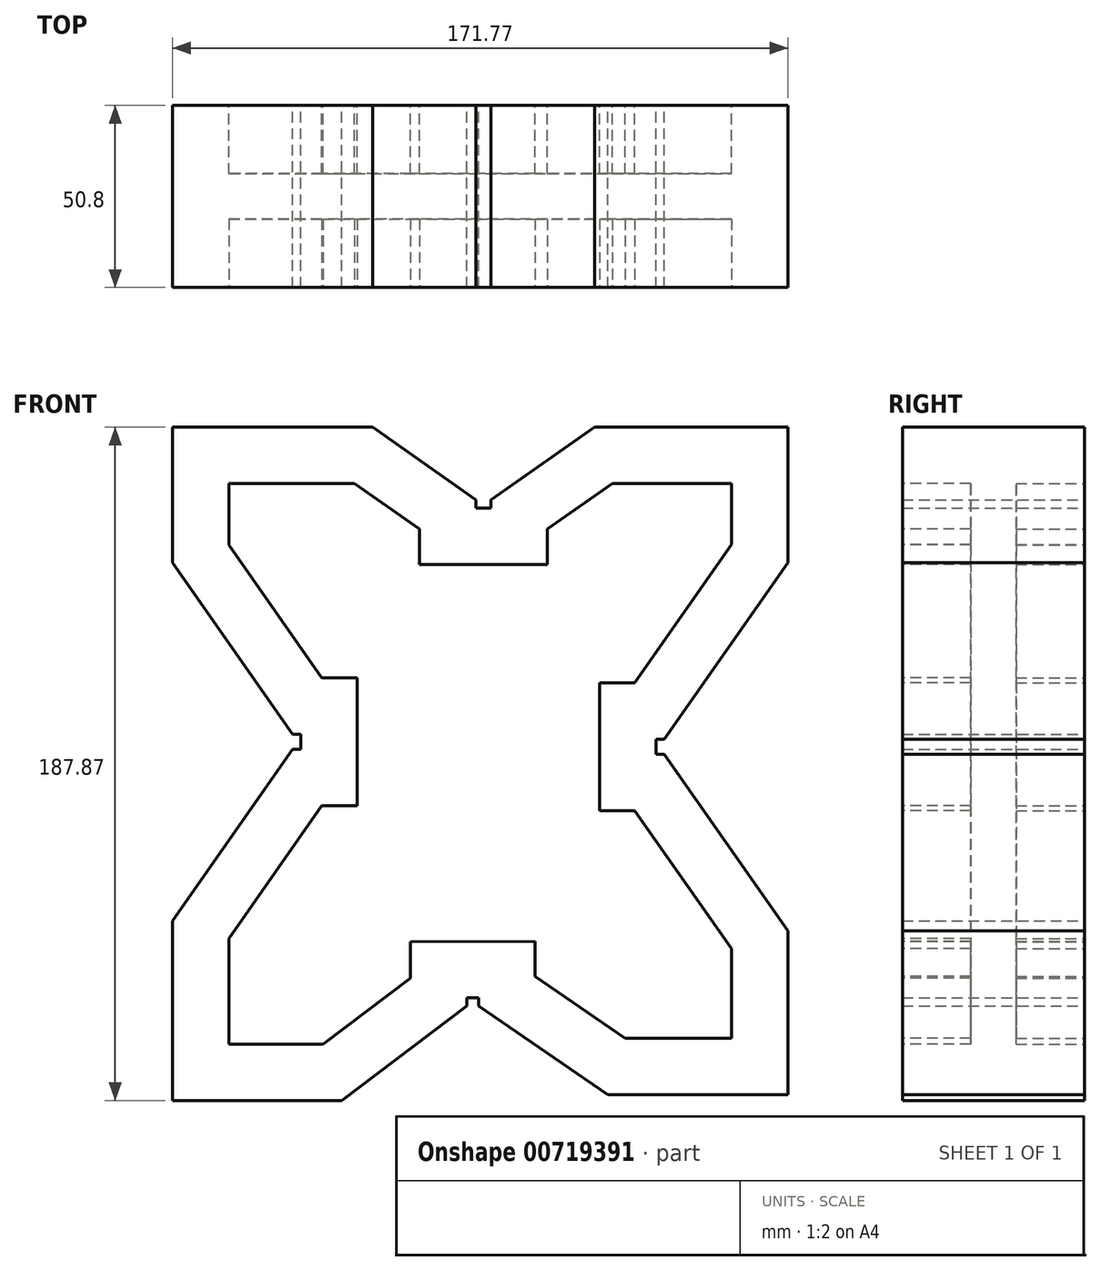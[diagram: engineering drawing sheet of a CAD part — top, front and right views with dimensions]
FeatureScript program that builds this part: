
annotation { "Feature Type Name" : "Feature", "Feature Type Description" : "" }
export const myFeature = defineFeature(function(context is Context, id is Id, definition is map)
    precondition{}
    {
        {
            var Q0;
            Q0=qCreatedBy(makeId("Front.planeOp"),FACE);
            var sketch = newSketch(context, id + "F0", { "sketchPlane" : qUnion([Q0])});
            skLineSegment(sketch, "E0", {"start": v(0, 2.31) * mm, "end": v(-28.9, 22.55) * mm});
            skLineSegment(sketch, "E1", {"start": v(-28.9, 22.55) * mm, "end": v(-84.7, 22.55) * mm});
            skLineSegment(sketch, "E2", {"start": v(-84.7, 22.55) * mm, "end": v(-84.7, -15.3) * mm});
            skLineSegment(sketch, "E3", {"start": v(33.12, 22.55) * mm, "end": v(4.22, 2.31) * mm});
            skLineSegment(sketch, "E4", {"start": v(4.22, 2.31) * mm, "end": v(4.22, 0) * mm});
            skLineSegment(sketch, "E5", {"start": v(33.12, 22.55) * mm, "end": v(87.07, 22.55) * mm});
            skLineSegment(sketch, "E6", {"start": v(87.07, 22.55) * mm, "end": v(87.07, -15.2) * mm});
            skLineSegment(sketch, "E7", {"start": v(0, 2.31) * mm, "end": v(0, 0) * mm});
            skLineSegment(sketch, "E8", {"start": v(87.07, -15.2) * mm, "end": v(52.55, -64.49) * mm});
            skLineSegment(sketch, "E9", {"start": v(52.55, -64.49) * mm, "end": v(50.24, -64.49) * mm});
            skLineSegment(sketch, "E10", {"start": v(50.24, -68.7) * mm, "end": v(52.55, -68.7) * mm});
            skLineSegment(sketch, "E11", {"start": v(52.55, -68.7) * mm, "end": v(87.07, -118) * mm});
            skLineSegment(sketch, "E12", {"start": v(87.07, -118) * mm, "end": v(87.07, -163.77) * mm});
            skLineSegment(sketch, "E13", {"start": v(87.07, -163.77) * mm, "end": v(36.75, -163.77) * mm});
            skLineSegment(sketch, "E14", {"start": v(-48.9, -67.35) * mm, "end": v(-51.21, -67.35) * mm});
            skLineSegment(sketch, "E15", {"start": v(-51.21, -67.35) * mm, "end": v(-84.7, -115.18) * mm});
            skLineSegment(sketch, "E16", {"start": v(-84.7, -115.18) * mm, "end": v(-84.7, -165.32) * mm});
            skLineSegment(sketch, "E17", {"start": v(-84.7, -165.32) * mm, "end": v(-37.43, -165.32) * mm});
            skLineSegment(sketch, "E18", {"start": v(-37.43, -165.32) * mm, "end": v(-2.5, -139) * mm});
            skLineSegment(sketch, "E19", {"start": v(-2.5, -139) * mm, "end": v(-2.5, -136.69) * mm});
            skLineSegment(sketch, "E20", {"start": v(-84.7, -15.3) * mm, "end": v(-51.21, -63.13) * mm});
            skLineSegment(sketch, "E21", {"start": v(-51.21, -63.13) * mm, "end": v(-48.9, -63.13) * mm});
            skLineSegment(sketch, "E22", {"start": v(36.75, -163.77) * mm, "end": v(0.7, -139) * mm});
            skLineSegment(sketch, "E23", {"start": v(0.7, -139) * mm, "end": v(0.7, -136.68) * mm});
            skLineSegment(sketch, "E24", {"start": v(0, 0) * mm, "end": v(4.22, 0) * mm});
            skLineSegment(sketch, "E25", {"start": v(-2.5, -136.69) * mm, "end": v(0.7, -136.68) * mm});
            skLineSegment(sketch, "E26", {"start": v(-48.9, -63.13) * mm, "end": v(-48.9, -67.35) * mm});
            skLineSegment(sketch, "E27", {"start": v(50.24, -64.49) * mm, "end": v(50.24, -68.7) * mm});
            skSolve(sketch);
        }
        {
            var Q0;
            Q0=makeQuery(id+"F0.imprint","IMPRINT",FACE,{"disambiguationData":[TD([[makeQuery(id+"F0.imprint","IMPRINT",EDGE,{"derivedFrom":sQuery(id+"F0.wireOp",EDGE,"E0")}),1.0]])]});
            extrude(context, id + "F1", {"entities" : qUnion([Q0]), "endBound" : BoundingType.SYMMETRIC, "depth" : 50.8 * mm, "offsetDistance" : 25.4 * mm});
        }
        {
            var Q0;
            Q0=makeQuery(id+"F1.opExtrude","CAP_FACE",FACE,{"disambiguationData":[OSD([sQuery(id+"F0.wireOp",EDGE,"E0"),sQuery(id+"F0.wireOp",EDGE,"E1"),sQuery(id+"F0.wireOp",EDGE,"E2"),sQuery(id+"F0.wireOp",EDGE,"E3"),sQuery(id+"F0.wireOp",EDGE,"E4"),sQuery(id+"F0.wireOp",EDGE,"E5"),sQuery(id+"F0.wireOp",EDGE,"E6"),sQuery(id+"F0.wireOp",EDGE,"E7"),sQuery(id+"F0.wireOp",EDGE,"E8"),sQuery(id+"F0.wireOp",EDGE,"E9"),sQuery(id+"F0.wireOp",EDGE,"E10"),sQuery(id+"F0.wireOp",EDGE,"E11"),sQuery(id+"F0.wireOp",EDGE,"E12"),sQuery(id+"F0.wireOp",EDGE,"E13"),sQuery(id+"F0.wireOp",EDGE,"E14"),sQuery(id+"F0.wireOp",EDGE,"E15"),sQuery(id+"F0.wireOp",EDGE,"E16"),sQuery(id+"F0.wireOp",EDGE,"E17"),sQuery(id+"F0.wireOp",EDGE,"E18"),sQuery(id+"F0.wireOp",EDGE,"E19"),sQuery(id+"F0.wireOp",EDGE,"E20"),sQuery(id+"F0.wireOp",EDGE,"E21"),sQuery(id+"F0.wireOp",EDGE,"E22"),sQuery(id+"F0.wireOp",EDGE,"E23"),sQuery(id+"F0.wireOp",EDGE,"E24"),sQuery(id+"F0.wireOp",EDGE,"E25"),sQuery(id+"F0.wireOp",EDGE,"E26"),sQuery(id+"F0.wireOp",EDGE,"E27")])],"isStart":false});
            var sketch = newSketch(context, id + "F2", { "sketchPlane" : qUnion([Q0])});
            skLineSegment(sketch, "E28.0", {"start": v(33.12, 22.55) * mm, "end": v(4.22, 2.31) * mm});
            skLineSegment(sketch, "E29.0", {"start": v(33.12, 22.55) * mm, "end": v(87.07, 22.55) * mm});
            skLineSegment(sketch, "E30.0", {"start": v(87.07, 22.55) * mm, "end": v(87.07, -15.2) * mm});
            skLineSegment(sketch, "E31.0", {"start": v(87.07, -15.2) * mm, "end": v(52.55, -64.49) * mm});
            skLineSegment(sketch, "E32.0.0", {"start": v(0.7, -139) * mm, "end": v(36.75, -163.77) * mm});
            skLineSegment(sketch, "E32.0.1", {"start": v(36.75, -163.77) * mm, "end": v(87.07, -163.77) * mm});
            skLineSegment(sketch, "E32.0.2", {"start": v(87.07, -163.77) * mm, "end": v(87.07, -118) * mm});
            skLineSegment(sketch, "E32.0.3", {"start": v(87.07, -118) * mm, "end": v(52.55, -68.7) * mm});
            skLineSegment(sketch, "E32.0.4", {"start": v(52.55, -68.7) * mm, "end": v(50.24, -68.7) * mm});
            skLineSegment(sketch, "E32.0.5", {"start": v(50.24, -68.7) * mm, "end": v(50.24, -64.49) * mm});
            skLineSegment(sketch, "E32.0.6", {"start": v(50.24, -64.49) * mm, "end": v(52.55, -64.49) * mm});
            skLineSegment(sketch, "E32.0.7", {"start": v(52.55, -64.49) * mm, "end": v(87.07, -15.2) * mm});
            skLineSegment(sketch, "E32.0.8", {"start": v(87.07, -15.2) * mm, "end": v(87.07, 22.55) * mm});
            skLineSegment(sketch, "E32.0.9", {"start": v(87.07, 22.55) * mm, "end": v(33.12, 22.55) * mm});
            skLineSegment(sketch, "E32.0.11", {"start": v(4.22, 2.31) * mm, "end": v(4.22, 0) * mm});
            skLineSegment(sketch, "E32.0.12", {"start": v(4.22, 0) * mm, "end": v(0, 0) * mm});
            skLineSegment(sketch, "E32.0.13", {"start": v(0, 0) * mm, "end": v(0, 2.31) * mm});
            skLineSegment(sketch, "E32.0.14", {"start": v(0, 2.31) * mm, "end": v(-28.9, 22.55) * mm});
            skLineSegment(sketch, "E32.0.15", {"start": v(-28.9, 22.55) * mm, "end": v(-84.7, 22.55) * mm});
            skLineSegment(sketch, "E32.0.16", {"start": v(-84.7, 22.55) * mm, "end": v(-84.7, -15.3) * mm});
            skLineSegment(sketch, "E32.0.17", {"start": v(-84.7, -15.3) * mm, "end": v(-51.21, -63.13) * mm});
            skLineSegment(sketch, "E32.0.18", {"start": v(-51.21, -63.13) * mm, "end": v(-48.9, -63.13) * mm});
            skLineSegment(sketch, "E32.0.19", {"start": v(-48.9, -63.13) * mm, "end": v(-48.9, -67.35) * mm});
            skLineSegment(sketch, "E32.0.20", {"start": v(-48.9, -67.35) * mm, "end": v(-51.21, -67.35) * mm});
            skLineSegment(sketch, "E32.0.21", {"start": v(-51.21, -67.35) * mm, "end": v(-84.7, -115.18) * mm});
            skLineSegment(sketch, "E32.0.22", {"start": v(-84.7, -115.18) * mm, "end": v(-84.7, -165.32) * mm});
            skLineSegment(sketch, "E32.0.23", {"start": v(-84.7, -165.32) * mm, "end": v(-37.43, -165.32) * mm});
            skLineSegment(sketch, "E32.0.24", {"start": v(-37.43, -165.32) * mm, "end": v(-2.5, -139) * mm});
            skLineSegment(sketch, "E32.0.25", {"start": v(-2.5, -139) * mm, "end": v(-2.5, -136.69) * mm});
            skLineSegment(sketch, "E32.0.26", {"start": v(-2.5, -136.69) * mm, "end": v(0.7, -136.68) * mm});
            skLineSegment(sketch, "E32.0.27", {"start": v(0.7, -136.68) * mm, "end": v(0.7, -139) * mm});
            skLineSegment(sketch, "E33.0", {"start": v(16.45, -120.89) * mm, "end": v(16.45, -130.7) * mm});
            skLineSegment(sketch, "E33.1", {"start": v(-18.25, -120.98) * mm, "end": v(16.45, -120.89) * mm});
            skLineSegment(sketch, "E33.2", {"start": v(-18.25, -131.15) * mm, "end": v(-18.25, -120.98) * mm});
            skLineSegment(sketch, "E33.3", {"start": v(-42.7, -149.57) * mm, "end": v(-18.25, -131.15) * mm});
            skLineSegment(sketch, "E33.4", {"start": v(-68.96, -149.57) * mm, "end": v(-42.7, -149.57) * mm});
            skLineSegment(sketch, "E33.5", {"start": v(38.08, 6.8) * mm, "end": v(19.96, -5.89) * mm});
            skLineSegment(sketch, "E33.6", {"start": v(71.32, 6.8) * mm, "end": v(38.08, 6.8) * mm});
            skLineSegment(sketch, "E33.7", {"start": v(71.32, -10.23) * mm, "end": v(71.32, 6.8) * mm});
            skLineSegment(sketch, "E33.8", {"start": v(44.35, -48.74) * mm, "end": v(71.32, -10.23) * mm});
            skLineSegment(sketch, "E33.9", {"start": v(34.5, -48.74) * mm, "end": v(44.35, -48.74) * mm});
            skLineSegment(sketch, "E33.10", {"start": v(34.5, -84.45) * mm, "end": v(34.5, -48.74) * mm});
            skLineSegment(sketch, "E33.11", {"start": v(41.64, -148.02) * mm, "end": v(71.32, -148.02) * mm});
            skLineSegment(sketch, "E33.12", {"start": v(71.32, -148.02) * mm, "end": v(71.32, -122.96) * mm});
            skLineSegment(sketch, "E33.13", {"start": v(71.32, -122.96) * mm, "end": v(44.35, -84.45) * mm});
            skLineSegment(sketch, "E33.14", {"start": v(44.35, -84.45) * mm, "end": v(34.5, -84.45) * mm});
            skLineSegment(sketch, "E33.15", {"start": v(19.96, -5.89) * mm, "end": v(19.96, -15.75) * mm});
            skLineSegment(sketch, "E33.16", {"start": v(19.96, -15.75) * mm, "end": v(-15.75, -15.75) * mm});
            skLineSegment(sketch, "E33.17", {"start": v(-15.75, -15.75) * mm, "end": v(-15.75, -5.89) * mm});
            skLineSegment(sketch, "E33.18", {"start": v(-15.75, -5.89) * mm, "end": v(-33.87, 6.8) * mm});
            skLineSegment(sketch, "E33.19", {"start": v(-33.87, 6.8) * mm, "end": v(-68.96, 6.8) * mm});
            skLineSegment(sketch, "E33.20", {"start": v(16.45, -130.7) * mm, "end": v(41.64, -148.02) * mm});
            skLineSegment(sketch, "E33.21", {"start": v(-68.96, 6.8) * mm, "end": v(-68.96, -10.33) * mm});
            skLineSegment(sketch, "E33.22", {"start": v(-68.96, -10.33) * mm, "end": v(-43.01, -47.38) * mm});
            skLineSegment(sketch, "E33.23", {"start": v(-43.01, -47.38) * mm, "end": v(-33.15, -47.38) * mm});
            skLineSegment(sketch, "E33.24", {"start": v(-33.15, -47.38) * mm, "end": v(-33.15, -83.1) * mm});
            skLineSegment(sketch, "E33.25", {"start": v(-33.15, -83.1) * mm, "end": v(-43.01, -83.1) * mm});
            skLineSegment(sketch, "E33.26", {"start": v(-43.01, -83.1) * mm, "end": v(-68.96, -120.15) * mm});
            skLineSegment(sketch, "E33.27", {"start": v(-68.96, -120.15) * mm, "end": v(-68.96, -149.57) * mm});
            skSolve(sketch);
        }
        {
            var Q0;
            Q0=makeQuery(id+"F2.imprint","IMPRINT",FACE,{"disambiguationData":[TD([[makeQuery(id+"F2.imprint","IMPRINT",EDGE,{"derivedFrom":sQuery(id+"F2.wireOp",EDGE,"E33.0")}),1.0]])]});
            extrude(context, id + "F3", {"entities" : qUnion([Q0]), "operationType" : NewBodyOperationType.REMOVE, "oppositeDirection" : true, "depth" : 19.05 * mm, "offsetDistance" : 25.4 * mm});
        }
        {
            var Q0;
            Q0=makeQuery(id+"F1.opExtrude","CAP_FACE",FACE,{"disambiguationData":[OSD([sQuery(id+"F0.wireOp",EDGE,"E0"),sQuery(id+"F0.wireOp",EDGE,"E1"),sQuery(id+"F0.wireOp",EDGE,"E2"),sQuery(id+"F0.wireOp",EDGE,"E3"),sQuery(id+"F0.wireOp",EDGE,"E4"),sQuery(id+"F0.wireOp",EDGE,"E5"),sQuery(id+"F0.wireOp",EDGE,"E6"),sQuery(id+"F0.wireOp",EDGE,"E7"),sQuery(id+"F0.wireOp",EDGE,"E8"),sQuery(id+"F0.wireOp",EDGE,"E9"),sQuery(id+"F0.wireOp",EDGE,"E10"),sQuery(id+"F0.wireOp",EDGE,"E11"),sQuery(id+"F0.wireOp",EDGE,"E12"),sQuery(id+"F0.wireOp",EDGE,"E13"),sQuery(id+"F0.wireOp",EDGE,"E14"),sQuery(id+"F0.wireOp",EDGE,"E15"),sQuery(id+"F0.wireOp",EDGE,"E16"),sQuery(id+"F0.wireOp",EDGE,"E17"),sQuery(id+"F0.wireOp",EDGE,"E18"),sQuery(id+"F0.wireOp",EDGE,"E19"),sQuery(id+"F0.wireOp",EDGE,"E20"),sQuery(id+"F0.wireOp",EDGE,"E21"),sQuery(id+"F0.wireOp",EDGE,"E22"),sQuery(id+"F0.wireOp",EDGE,"E23"),sQuery(id+"F0.wireOp",EDGE,"E24"),sQuery(id+"F0.wireOp",EDGE,"E25"),sQuery(id+"F0.wireOp",EDGE,"E26"),sQuery(id+"F0.wireOp",EDGE,"E27")])],"isStart":true});
            var sketch = newSketch(context, id + "F4", { "sketchPlane" : qUnion([Q0])});
            skLineSegment(sketch, "E34.0.0", {"start": v(-36.75, -163.77) * mm, "end": v(-0.7, -139) * mm});
            skLineSegment(sketch, "E34.0.1", {"start": v(-0.7, -139) * mm, "end": v(-0.7, -136.68) * mm});
            skLineSegment(sketch, "E34.0.2", {"start": v(-0.7, -136.68) * mm, "end": v(2.5, -136.69) * mm});
            skLineSegment(sketch, "E34.0.3", {"start": v(2.5, -136.69) * mm, "end": v(2.5, -139) * mm});
            skLineSegment(sketch, "E34.0.4", {"start": v(2.5, -139) * mm, "end": v(37.43, -165.32) * mm});
            skLineSegment(sketch, "E34.0.5", {"start": v(37.43, -165.32) * mm, "end": v(84.7, -165.32) * mm});
            skLineSegment(sketch, "E34.0.6", {"start": v(84.7, -165.32) * mm, "end": v(84.7, -115.18) * mm});
            skLineSegment(sketch, "E34.0.7", {"start": v(84.7, -115.18) * mm, "end": v(51.21, -67.35) * mm});
            skLineSegment(sketch, "E34.0.8", {"start": v(51.21, -67.35) * mm, "end": v(48.9, -67.35) * mm});
            skLineSegment(sketch, "E34.0.9", {"start": v(48.9, -67.35) * mm, "end": v(48.9, -63.13) * mm});
            skLineSegment(sketch, "E34.0.10", {"start": v(48.9, -63.13) * mm, "end": v(51.21, -63.13) * mm});
            skLineSegment(sketch, "E34.0.11", {"start": v(51.21, -63.13) * mm, "end": v(84.7, -15.3) * mm});
            skLineSegment(sketch, "E34.0.12", {"start": v(84.7, -15.3) * mm, "end": v(84.7, 22.55) * mm});
            skLineSegment(sketch, "E34.0.13", {"start": v(84.7, 22.55) * mm, "end": v(28.9, 22.55) * mm});
            skLineSegment(sketch, "E34.0.14", {"start": v(28.9, 22.55) * mm, "end": v(0, 2.31) * mm});
            skLineSegment(sketch, "E34.0.15", {"start": v(0, 2.31) * mm, "end": v(0, 0) * mm});
            skLineSegment(sketch, "E34.0.16", {"start": v(0, 0) * mm, "end": v(-4.22, 0) * mm});
            skLineSegment(sketch, "E34.0.17", {"start": v(-4.22, 0) * mm, "end": v(-4.22, 2.31) * mm});
            skLineSegment(sketch, "E34.0.18", {"start": v(-4.22, 2.31) * mm, "end": v(-33.12, 22.55) * mm});
            skLineSegment(sketch, "E34.0.19", {"start": v(-33.12, 22.55) * mm, "end": v(-87.07, 22.55) * mm});
            skLineSegment(sketch, "E34.0.20", {"start": v(-87.07, 22.55) * mm, "end": v(-87.07, -15.2) * mm});
            skLineSegment(sketch, "E34.0.21", {"start": v(-87.07, -15.2) * mm, "end": v(-52.55, -64.49) * mm});
            skLineSegment(sketch, "E34.0.22", {"start": v(-52.55, -64.49) * mm, "end": v(-50.24, -64.49) * mm});
            skLineSegment(sketch, "E34.0.23", {"start": v(-50.24, -64.49) * mm, "end": v(-50.24, -68.7) * mm});
            skLineSegment(sketch, "E34.0.24", {"start": v(-50.24, -68.7) * mm, "end": v(-52.55, -68.7) * mm});
            skLineSegment(sketch, "E34.0.25", {"start": v(-52.55, -68.7) * mm, "end": v(-87.07, -118) * mm});
            skLineSegment(sketch, "E34.0.26", {"start": v(-87.07, -118) * mm, "end": v(-87.07, -163.77) * mm});
            skLineSegment(sketch, "E34.0.27", {"start": v(-87.07, -163.77) * mm, "end": v(-36.75, -163.77) * mm});
            skLineSegment(sketch, "E35.0", {"start": v(-71.32, -148.02) * mm, "end": v(-41.64, -148.02) * mm});
            skLineSegment(sketch, "E35.1", {"start": v(-71.32, -122.96) * mm, "end": v(-71.32, -148.02) * mm});
            skLineSegment(sketch, "E35.2", {"start": v(-44.35, -84.45) * mm, "end": v(-71.32, -122.96) * mm});
            skLineSegment(sketch, "E35.3", {"start": v(-34.5, -84.45) * mm, "end": v(-44.35, -84.45) * mm});
            skLineSegment(sketch, "E35.4", {"start": v(-34.5, -48.74) * mm, "end": v(-34.5, -84.45) * mm});
            skLineSegment(sketch, "E35.5", {"start": v(33.15, -47.38) * mm, "end": v(43.01, -47.38) * mm});
            skLineSegment(sketch, "E35.6", {"start": v(33.15, -83.1) * mm, "end": v(33.15, -47.38) * mm});
            skLineSegment(sketch, "E35.7", {"start": v(43.01, -83.1) * mm, "end": v(33.15, -83.1) * mm});
            skLineSegment(sketch, "E35.8", {"start": v(68.96, -120.15) * mm, "end": v(43.01, -83.1) * mm});
            skLineSegment(sketch, "E35.9", {"start": v(68.96, -149.57) * mm, "end": v(68.96, -120.15) * mm});
            skLineSegment(sketch, "E35.10", {"start": v(42.7, -149.57) * mm, "end": v(68.96, -149.57) * mm});
            skLineSegment(sketch, "E35.11", {"start": v(-16.45, -130.7) * mm, "end": v(-16.45, -120.89) * mm});
            skLineSegment(sketch, "E35.12", {"start": v(-16.45, -120.89) * mm, "end": v(18.25, -120.98) * mm});
            skLineSegment(sketch, "E35.13", {"start": v(18.25, -120.98) * mm, "end": v(18.25, -131.15) * mm});
            skLineSegment(sketch, "E35.14", {"start": v(18.25, -131.15) * mm, "end": v(42.7, -149.57) * mm});
            skLineSegment(sketch, "E35.15", {"start": v(43.01, -47.38) * mm, "end": v(68.96, -10.33) * mm});
            skLineSegment(sketch, "E35.16", {"start": v(68.96, -10.33) * mm, "end": v(68.96, 6.8) * mm});
            skLineSegment(sketch, "E35.17", {"start": v(68.96, 6.8) * mm, "end": v(33.87, 6.8) * mm});
            skLineSegment(sketch, "E35.18", {"start": v(33.87, 6.8) * mm, "end": v(15.75, -5.89) * mm});
            skLineSegment(sketch, "E35.19", {"start": v(15.75, -5.89) * mm, "end": v(15.75, -15.75) * mm});
            skLineSegment(sketch, "E35.20", {"start": v(-41.64, -148.02) * mm, "end": v(-16.45, -130.7) * mm});
            skLineSegment(sketch, "E35.21", {"start": v(15.75, -15.75) * mm, "end": v(-19.96, -15.75) * mm});
            skLineSegment(sketch, "E35.22", {"start": v(-19.96, -15.75) * mm, "end": v(-19.96, -5.89) * mm});
            skLineSegment(sketch, "E35.23", {"start": v(-19.96, -5.89) * mm, "end": v(-38.08, 6.8) * mm});
            skLineSegment(sketch, "E35.24", {"start": v(-38.08, 6.8) * mm, "end": v(-71.32, 6.8) * mm});
            skLineSegment(sketch, "E35.25", {"start": v(-71.32, 6.8) * mm, "end": v(-71.32, -10.23) * mm});
            skLineSegment(sketch, "E35.26", {"start": v(-71.32, -10.23) * mm, "end": v(-44.35, -48.74) * mm});
            skLineSegment(sketch, "E35.27", {"start": v(-44.35, -48.74) * mm, "end": v(-34.5, -48.74) * mm});
            skSolve(sketch);
        }
        {
            var Q0;
            Q0=makeQuery(id+"F4.imprint","IMPRINT",FACE,{"disambiguationData":[TD([[makeQuery(id+"F4.imprint","IMPRINT",EDGE,{"derivedFrom":sQuery(id+"F4.wireOp",EDGE,"E35.0")}),1.0]])]});
            extrude(context, id + "F5", {"entities" : qUnion([Q0]), "operationType" : NewBodyOperationType.REMOVE, "oppositeDirection" : true, "depth" : 19.05 * mm, "offsetDistance" : 25.4 * mm});
        }
    });
